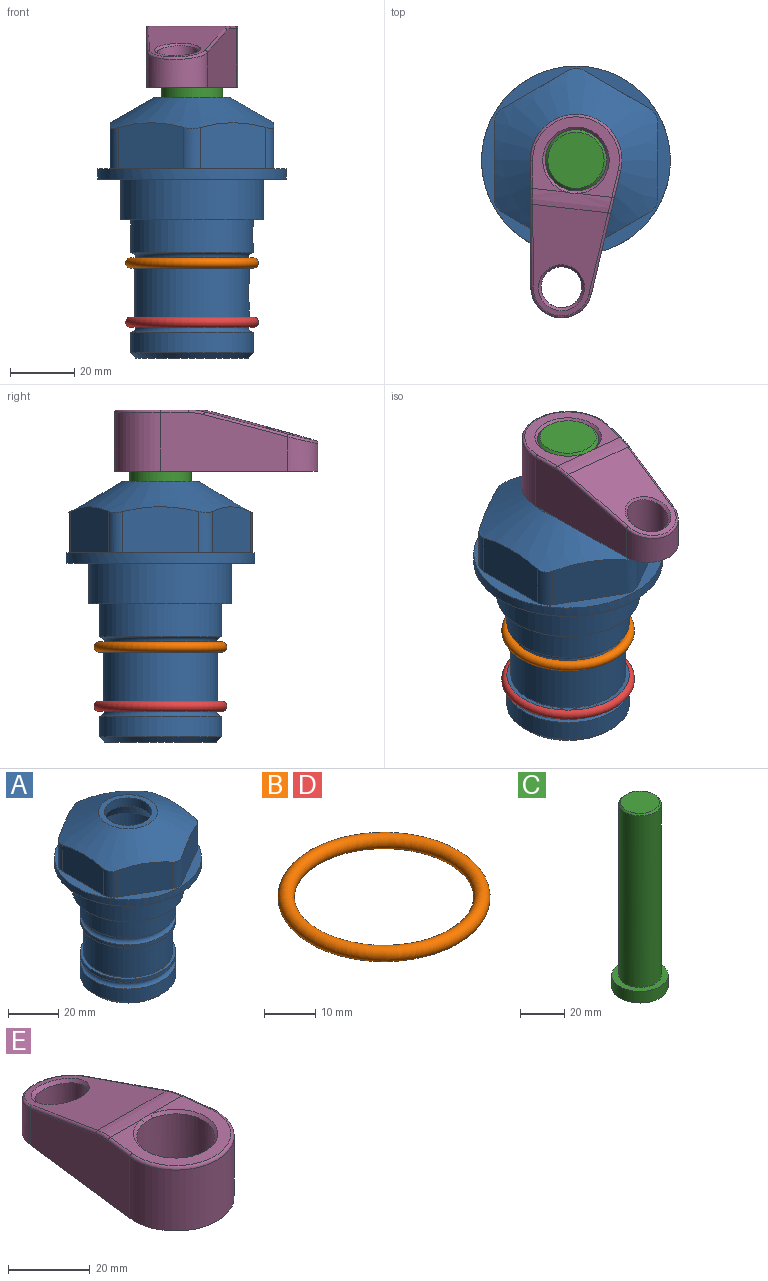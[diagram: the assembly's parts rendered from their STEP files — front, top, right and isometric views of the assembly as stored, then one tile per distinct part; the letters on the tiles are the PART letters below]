
ASSEMBLY  parts=5 mates=4
PART A: 36 faces, bbox 58.7x58.7x81 mm
  f0: cylinder r=17.78mm len=35.56mm, axis (0,0,1), area 1670.8mm2, adj f23,f24,f31
  f1: cylinder r=19.05mm len=38.1mm, axis (0,0,1), area 1191.9mm2, adj f26,f27,f30
  f2: plane 58.66x58.66mm, normal (0,0,-1), area 1150.6mm2, adj f3,f28
  f3: cylinder r=29.33mm len=58.66mm, axis (0,0,-1), area 585.1mm2, adj f2,f4
  f4: plane 58.66x58.66mm, normal (0,0,1), area 475.9mm2, adj f3,f5,f6,f7,f8,f9,f10,f11
  f5: plane 20.32x14.34mm, normal (-0.5,0.87,0), area 324.4mm2, adj f4,f15,f16,f17
  f6: plane 20.32x14.34mm, normal (0.5,0.87,0), area 324.4mm2, adj f4,f14,f15,f17
  f7: plane 23.48x14.34mm, normal (1,0,0), area 324.4mm2, adj f4,f13,f14,f17
  f8: plane 20.32x14.34mm, normal (0.5,-0.87,0), area 324.4mm2, adj f4,f12,f13,f17
  f9: plane 20.32x14.34mm, normal (-0.5,-0.87,0), area 324.4mm2, adj f4,f11,f12,f17
  f10: plane 23.48x14.34mm, normal (-1,0,0), area 324.4mm2, adj f4,f11,f16,f17
  f11: cylinder r=5.08mm len=12.85mm, axis (0,0,-1), area 67.2mm2, adj f4,f9,f10,f17
  f12: cylinder r=5.08mm len=12.85mm, axis (0,0,-1), area 67.2mm2, adj f4,f8,f9,f17
  f13: cylinder r=5.08mm len=12.85mm, axis (0,0,-1), area 67.2mm2, adj f4,f7,f8,f17
  f14: cylinder r=5.08mm len=12.85mm, axis (0,0,-1), area 67.2mm2, adj f4,f6,f7,f17
  f15: cylinder r=5.08mm len=12.85mm, axis (0,0,-1), area 67.2mm2, adj f4,f5,f6,f17
  f16: cylinder r=5.08mm len=12.85mm, axis (0,0,-1), area 67.2mm2, adj f4,f5,f10,f17
  f17: cone r=11.73mm half-angle=60deg, axis (0,0,-1), area 2071.8mm2, adj f5,f6,f7,f8,f9,f10,f11,f12
  f18: plane 23.46x23.46mm, normal (0,0,1), area 147.4mm2, adj f17,f35
  f19: plane 34.93x34.93mm, normal (0,0,-1), area 958mm2, adj f29
  f20: cylinder r=19.05mm len=38.1mm, axis (0,0,1), area 760.1mm2, adj f21,f29
  f21: torus R=19.05mm, axis (0,0,1), area 565.3mm2, adj f20,f22
  f22: cylinder r=19.05mm len=38.1mm, axis (0,0,1), area 190mm2, adj f21,f23
  f23: plane 38.1x38.1mm, normal (0,0,1), area 146.9mm2, adj f0,f22
  f24: plane 38.1x38.1mm, normal (0,0,-1), area 146.9mm2, adj f0,f25
  f25: cylinder r=19.05mm len=38.1mm, axis (0,0,1), area 190mm2, adj f24,f26
  f26: torus R=19.05mm, axis (0,0,1), area 565.3mm2, adj f1,f25
  f27: plane 44.45x44.45mm, normal (0,0,-1), area 411.7mm2, adj f1,f28
  f28: cylinder r=22.23mm len=44.45mm, axis (0,0,1), area 1773.5mm2, adj f2,f27
  f29: cone r=19.05mm half-angle=45deg, axis (0,0,1), area 257.5mm2, adj f19,f20
  f30: cylinder r=3.17mm len=6.75mm, axis (-1,0,0), area 128mm2, adj f1,f33
  f31: cylinder r=3.17mm len=6.35mm, axis (-1,0,0), area 102.5mm2, adj f0,f33
  f32: plane 25.4x25.4mm, normal (0,0,1), area 506.7mm2, adj f33
  f33: cylinder r=12.7mm len=66.42mm, axis (0,0,-1), area 5236.2mm2, adj f30,f31,f32,f34
  f34: cone r=9.53mm half-angle=30deg, axis (0,0,-1), area 443.4mm2, adj f33,f35
  f35: cylinder r=9.53mm len=19.05mm, axis (0,0,-1), area 240.9mm2, adj f18,f34
PART B: 1 faces, bbox 44.7x44.7x3.2 mm
  f0: torus R=19.05mm, axis (0,0,1), area 1193.9mm2
PART C: 6 faces, bbox 25.4x25.4x101.6 mm
  f0: plane 17.46x17.46mm, normal (0,0,1), area 239.5mm2, adj f5
  f1: plane 25.4x25.4mm, normal (0,0,-1), area 506.7mm2, adj f2
  f2: cylinder r=12.7mm len=25.4mm, axis (0,0,1), area 506.7mm2, adj f1,f3
  f3: plane 25.4x25.4mm, normal (0,0,1), area 221.7mm2, adj f2,f4
  f4: cylinder r=9.53mm len=94.46mm, axis (0,0,1), area 5653mm2, adj f3,f5
  f5: cone r=8.73mm half-angle=45deg, axis (0,0,-1), area 64.4mm2, adj f0,f4
PART D: same geometry as B
PART E: 31 faces, bbox 31.7x65.5x19.8 mm
  f0: plane 39.12x18.26mm, normal (0.99,0.12,0), area 612.2mm2, adj f1,f4,f7,f11,f13,f15
  f1: cylinder r=9.53mm len=18.91mm, axis (0,0,-1), area 296.1mm2, adj f0,f2,f7,f17
  f2: plane 39.12x18.26mm, normal (-0.99,0.12,0), area 612.2mm2, adj f1,f4,f7,f12,f14,f16
  f3: cylinder r=6.35mm len=12.7mm, axis (0,0,-1), area 362.4mm2, adj f7,f18
  f4: cylinder r=14.29mm len=28.58mm, axis (0,0,-1), area 882.2mm2, adj f0,f2,f7,f10
  f5: cylinder r=9.53mm len=19.05mm, axis (0,0,-1), area 1092.6mm2, adj f7,f19,f20
  f6: plane 26.99x23.69mm, normal (0,0,1), area 216.2mm2, adj f9,f10,f11,f12,f19
  f7: plane 63.5x28.58mm, normal (0,0,-1), area 661.8mm2, adj f0,f1,f2,f3,f4,f5,f22,f23
  f8: plane 33.52x23.6mm, normal (0,0.26,0.97), area 486mm2, adj f9,f15,f16,f17,f18
  f9: cylinder r=19.05mm len=24.72mm, axis (1,0,0), area 120.4mm2, adj f6,f8,f13,f14,f20
  f10: torus R=13.49mm, axis (0,0,1), area 59mm2, adj f4,f6,f11,f12
  f11: cylinder r=0.79mm len=8.67mm, axis (0.12,-0.99,0), area 10.8mm2, adj f0,f6,f10,f13
  f12: cylinder r=0.79mm len=8.67mm, axis (0.12,0.99,0), area 10.8mm2, adj f2,f6,f10,f14
  f13: bspline ~4.95x1.42mm, area 6.1mm2, adj f0,f9,f11,f15
  f14: bspline ~4.95x1.42mm, area 6.1mm2, adj f2,f9,f12,f16
  f15: cylinder r=0.79mm len=25.95mm, axis (0.12,-0.96,0.26), area 32.9mm2, adj f0,f8,f13,f17
  f16: cylinder r=0.79mm len=25.95mm, axis (0.12,0.96,-0.26), area 32.9mm2, adj f2,f8,f14,f17
  f17: bspline ~18.91x8.38mm, area 30mm2, adj f1,f8,f15,f16
  f18: bspline ~14.29x14.29mm, area 48.3mm2, adj f3,f8
  f19: cone r=9.53mm half-angle=45deg, axis (0,0,1), area 66.5mm2, adj f5,f6,f20
  f20: bspline ~3.22x0.96mm, area 3.5mm2, adj f5,f9,f19
  f21: plane 2.75x2.72mm, normal (0,0,-1), area 2.9mm2, adj f23,f25,f28
  f22: plane 23.05x15.88mm, normal (-0.99,-0.12,0), area 323.6mm2, adj f7,f25,f26,f27,f28,f29
  f23: plane 23.05x15.88mm, normal (0.99,-0.12,0), area 323.6mm2, adj f7,f21,f25,f27,f28,f30
  f24: cylinder r=9.53mm len=10.69mm, axis (0,0,-1), area 114.7mm2, adj f7,f27,f29,f30
  f25: cylinder r=12.7mm len=20.59mm, axis (0,0,-1), area 381.1mm2, adj f7,f21,f22,f23,f26,f28
  f26: plane 2.75x2.72mm, normal (0,0,-1), area 2.9mm2, adj f22,f25,f28
  f27: plane 19.72x18.37mm, normal (0,-0.26,-0.97), area 291.8mm2, adj f22,f23,f24,f28,f29,f30
  f28: cylinder r=15.88mm len=19.92mm, axis (1,0,0), area 54.8mm2, adj f21,f22,f23,f25,f26,f27
  f29: cylinder r=1.59mm len=11mm, axis (0,0,-1), area 34.7mm2, adj f7,f22,f24,f27
  f30: cylinder r=1.59mm len=11mm, axis (0,0,-1), area 34.7mm2, adj f7,f23,f24,f27
PLACE A at identity fixed
PLACE B t=(0,0,-1.59)mm
PLACE C rot(axis=(0,0,1),173.5deg) t=(0,0,-15.94)mm
PLACE D t=(0,0,-20)mm
PLACE E rot(axis=(0,0,1),173.5deg) t=(0,0,-15.94)mm
MATE fastened C.f2 <-> E.f4  axis (0,0,1) through (0,0,47.56)mm
MATE fastened B.f0 <-> A.f0  axis (0,0,1) through (0,0,-26.1)mm
MATE fastened D.f0 <-> A.f0  axis (0,0,1) through (0,0,-44.51)mm
MATE cylindrical C.f2 <-> A.f0  axis (0,0,-1) through (0,0,-54.04)mm
